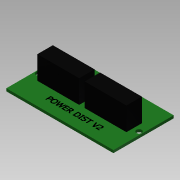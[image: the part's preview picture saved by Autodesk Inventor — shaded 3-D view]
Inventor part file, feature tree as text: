
AUTODESK INVENTOR PART (.ipt)
format: ipt  version: 2015 SP1 (Build 190203100, 203)  size: 104,448 bytes
history: native  units: mm
features: sketch x2, extrude x2
ambient origin geometry x8: Origin, YZ Plane, XZ Plane, XY Plane, X Axis, Y Axis, Z Axis, Center Point
bodies: Solid1 (feature_tree)
feature tree (4):
  sketch  "Sketch1"  dims[d0=69.215mm d1=38.989mm]
  extrude  "Extrusion1"  Depth=38.989mm
  extrude  "Extrusion2"  Depth=16.58mm
  sketch  "Sketch2"  dims[d2=3.5mm d3=2.172mm d4=20.216mm d5=27.0mm d6=10.0mm d14=1.7mm d15=0.0mm d16=16.58mm d17=0.0mm d18=64.884mm]
